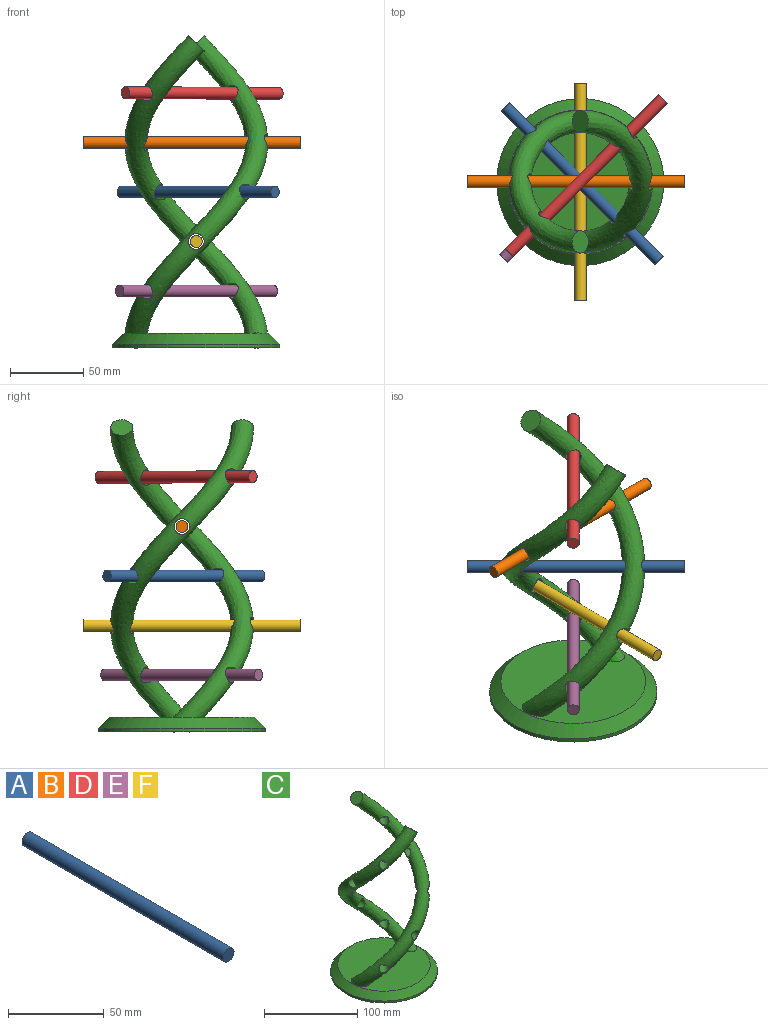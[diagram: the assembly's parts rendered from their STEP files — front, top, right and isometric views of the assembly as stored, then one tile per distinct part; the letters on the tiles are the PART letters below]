
ASSEMBLY  parts=6 mates=5
PART A: 3 faces, bbox 8.1x148.6x8.1 mm
  f0: cylinder r=4.06mm len=148.59mm, axis (0,1,0), area 3794.2mm2, adj f1,f2
  f1: plane 8.13x8.13mm, normal (0,-1,0), area 51.9mm2, adj f0
  f2: plane 8.13x8.13mm, normal (0,1,0), area 51.9mm2, adj f0
PART B: same geometry as A
PART C: 24 faces, bbox 116.4x116.4x221.1 mm
  f0: bspline ~213.65x97.64mm, area 12144.9mm2, adj f1,f2,f18,f19,f20,f21,f22,f23
  f1: plane 4.06x0.21mm, normal (0,0.69,-0.72), area 0.7mm2, adj f0,f2
  f2: plane 100.62x100.62mm, normal (0,0,1), area 7204.2mm2, adj f0,f1,f3,f10,f11
  f3: bspline ~213.65x97.77mm, area 12143.4mm2, adj f2,f4,f5,f6,f7,f8,f9,f10
  f4: cylinder r=5.4mm len=17.6mm, axis (-0.71,-0.71,0), area 452.6mm2, adj f3
  f5: cylinder r=5.4mm len=14.2mm, axis (0,1,0), area 473.9mm2, adj f3
  f6: plane 17.36x13.13mm, normal (0.69,0,0.72), area 182.4mm2, adj f3
  f7: cylinder r=5.4mm len=17.65mm, axis (-0.71,-0.71,0), area 454.3mm2, adj f3
  f8: cylinder r=5.4mm len=14.19mm, axis (1,0,0), area 473.6mm2, adj f3
  f9: cylinder r=5.4mm len=17.6mm, axis (0.71,-0.71,0), area 452.6mm2, adj f3
  f10: plane 4.06x0.21mm, normal (0,-0.69,-0.72), area 0.7mm2, adj f2,f3
  f11: cone r=49.53mm half-angle=45deg, axis (0,0,-1), area 3611.6mm2, adj f2,f12
  f12: cylinder r=57.15mm len=114.3mm, axis (0,0,-1), area 912.1mm2, adj f11,f13
  f13: plane 114.83x114.83mm, normal (0,0,-1), area 10258.8mm2, adj f12,f14,f15,f16,f17
  f14: plane 4.06x0.21mm, normal (0,-0.69,-0.72), area 0.7mm2, adj f13,f15
  f15: bspline ~24.34x22.85mm, area 0mm2, adj f13,f14
  f16: bspline ~24.34x22.85mm, area 0mm2, adj f13,f17
  f17: plane 4.06x0.21mm, normal (0,0.69,-0.72), area 0.7mm2, adj f13,f16
  f18: cylinder r=5.4mm len=17.72mm, axis (-0.71,-0.71,0), area 473.8mm2, adj f0
  f19: cylinder r=5.4mm len=14.37mm, axis (0,1,0), area 458.4mm2, adj f0
  f20: plane 17.36x13.13mm, normal (-0.69,0,0.72), area 182.4mm2, adj f0
  f21: cylinder r=5.4mm len=17.79mm, axis (-0.71,-0.71,0), area 456.3mm2, adj f0
  f22: cylinder r=5.4mm len=14.36mm, axis (1,0,0), area 458.1mm2, adj f0
  f23: cylinder r=5.4mm len=17.72mm, axis (0.71,-0.71,0), area 473.8mm2, adj f0
PART D: same geometry as A
PART E: same geometry as A
PART F: same geometry as A
PLACE A rot(axis=(0,0,1),45deg) t=(1.31,-1.31,106.69)mm
PLACE B rot(axis=(-0.58,0.58,0.58),120deg) t=(-2.92,0,140.55)mm
PLACE C t=(0,0,5.08)mm
PLACE D rot(axis=(-0.01,0,-1),45deg) t=(4.01,4.02,174.39)mm
PLACE E rot(axis=(0,0,-1),45deg) t=(0.18,0.18,38.95)mm
PLACE F t=(0,-6.88,72.81)mm
MATE slider F.f0 <-> C.f5  axis (0,1,0) through (0,-81.17,72.81)mm
MATE slider E.f0 <-> C.f4  axis (-0.71,-0.71,0) through (-52.36,-52.35,38.95)mm
MATE slider A.f0 <-> C.f9  axis (0.71,-0.71,0) through (53.85,-53.85,106.69)mm
MATE slider B.f0 <-> C.f8  axis (1,0,0) through (71.38,0,140.55)mm
MATE slider D.f0 <-> C.f7  axis (0.71,0.71,0) through (4.01,4.02,174.39)mm
